annotation { "Feature Type Name" : "Feature", "Feature Type Description" : "" }
export const myFeature = defineFeature(function(context is Context, id is Id, definition is map)
    precondition{}
    {
        {
            var Q0;
            Q0=qCreatedBy(makeId("Top.planeOp"),FACE);
            var sketch = newSketch(context, id + "F0", { "sketchPlane" : qUnion([Q0])});
            skLineSegment(sketch, "E0.bottom", {"start": v(40, -40) * mm, "end": v(-40, -40) * mm, "construction": true});
            skLineSegment(sketch, "E0.top", {"start": v(40, 40) * mm, "end": v(-40, 40) * mm, "construction": true});
            skLineSegment(sketch, "E0.left", {"start": v(40, -40) * mm, "end": v(40, 40) * mm, "construction": true});
            skLineSegment(sketch, "E0.right", {"start": v(-40, -40) * mm, "end": v(-40, 40) * mm, "construction": true});
            skPoint(sketch, "E0.middle", {"position": v(0, 0) * mm});
            skText(sketch, "E1", { "text": "HAPPY", "fontName": "OpenSans-Bold.ttf"});
            skText(sketch, "E2", { "text": "BIRTHDAY", "fontName": "OpenSans-Bold.ttf"});
            skText(sketch, "E3", { "text": "Lily Rose", "fontName": "OpenSans-Bold.ttf"});
            const initialGuessF0  = {"E1": [-0.0375, 0.01154, 1, 0, 0.01588], "E2": [-0.0375, -0.004, 1, 0, 0.01053], "E3": [-0.0375, -0.02129, 1, 0, 0.0123]};
            skSetInitialGuess(sketch, initialGuessF0);
            skSolve(sketch);
        }
        {
            var Q0;
            Q0=makeQuery(id+"F0.imprint","IMPRINT",FACE,{"disambiguationData":[TD([[makeQuery(id+"F0.imprint","IMPRINT",EDGE,{"derivedFrom":sQuery(id+"F0.wireOp",EDGE,"E1.sketch_text.stroke-40")}),-1.0]])]});
            var Q1;
            Q1=makeQuery(id+"F0.imprint","IMPRINT",FACE,{"disambiguationData":[TD([[makeQuery(id+"F0.imprint","IMPRINT",EDGE,{"derivedFrom":sQuery(id+"F0.wireOp",EDGE,"E1.sketch_text.stroke-56")}),-1.0]])]});
            var Q2;
            Q2=makeQuery(id+"F0.imprint","IMPRINT",FACE,{"disambiguationData":[TD([[makeQuery(id+"F0.imprint","IMPRINT",EDGE,{"derivedFrom":sQuery(id+"F0.wireOp",EDGE,"E2.sketch_text.stroke-0")}),-1.0]])]});
            var Q3;
            Q3=makeQuery(id+"F0.imprint","IMPRINT",FACE,{"disambiguationData":[TD([[makeQuery(id+"F0.imprint","IMPRINT",EDGE,{"derivedFrom":sQuery(id+"F0.wireOp",EDGE,"E1.sketch_text.stroke-0")}),-1.0]])]});
            var Q4;
            Q4=makeQuery(id+"F0.imprint","IMPRINT",FACE,{"disambiguationData":[TD([[makeQuery(id+"F0.imprint","IMPRINT",EDGE,{"derivedFrom":sQuery(id+"F0.wireOp",EDGE,"E1.sketch_text.stroke-12")}),-1.0]])]});
            var Q5;
            Q5=makeQuery(id+"F0.imprint","IMPRINT",FACE,{"disambiguationData":[TD([[makeQuery(id+"F0.imprint","IMPRINT",EDGE,{"derivedFrom":sQuery(id+"F0.wireOp",EDGE,"E1.sketch_text.stroke-24")}),-1.0]])]});
            var Q6;
            Q6=makeQuery(id+"F0.imprint","IMPRINT",FACE,{"disambiguationData":[TD([[makeQuery(id+"F0.imprint","IMPRINT",EDGE,{"derivedFrom":sQuery(id+"F0.wireOp",EDGE,"E2.sketch_text.stroke-25")}),-1.0]])]});
            var Q7;
            Q7=makeQuery(id+"F0.imprint","IMPRINT",FACE,{"disambiguationData":[TD([[makeQuery(id+"F0.imprint","IMPRINT",EDGE,{"derivedFrom":sQuery(id+"F0.wireOp",EDGE,"E2.sketch_text.stroke-29")}),-1.0]])]});
            var Q8;
            Q8=makeQuery(id+"F0.imprint","IMPRINT",FACE,{"disambiguationData":[TD([[makeQuery(id+"F0.imprint","IMPRINT",EDGE,{"derivedFrom":sQuery(id+"F0.wireOp",EDGE,"E2.sketch_text.stroke-48")}),-1.0]])]});
            var Q9;
            Q9=makeQuery(id+"F0.imprint","IMPRINT",FACE,{"disambiguationData":[TD([[makeQuery(id+"F0.imprint","IMPRINT",EDGE,{"derivedFrom":sQuery(id+"F0.wireOp",EDGE,"E2.sketch_text.stroke-56")}),-1.0]])]});
            var Q10;
            Q10=makeQuery(id+"F0.imprint","IMPRINT",FACE,{"disambiguationData":[TD([[makeQuery(id+"F0.imprint","IMPRINT",EDGE,{"derivedFrom":sQuery(id+"F0.wireOp",EDGE,"E2.sketch_text.stroke-68")}),-1.0]])]});
            var Q11;
            Q11=makeQuery(id+"F0.imprint","IMPRINT",FACE,{"disambiguationData":[TD([[makeQuery(id+"F0.imprint","IMPRINT",EDGE,{"derivedFrom":sQuery(id+"F0.wireOp",EDGE,"E2.sketch_text.stroke-80")}),-1.0]])]});
            var Q12;
            Q12=makeQuery(id+"F0.imprint","IMPRINT",FACE,{"disambiguationData":[TD([[makeQuery(id+"F0.imprint","IMPRINT",EDGE,{"derivedFrom":sQuery(id+"F0.wireOp",EDGE,"E2.sketch_text.stroke-92")}),-1.0]])]});
            var Q13;
            Q13=makeQuery(id+"F0.imprint","IMPRINT",FACE,{"disambiguationData":[TD([[makeQuery(id+"F0.imprint","IMPRINT",EDGE,{"derivedFrom":sQuery(id+"F0.wireOp",EDGE,"E3.sketch_text.stroke-0")}),-1.0]])]});
            var Q14;
            Q14=makeQuery(id+"F0.imprint","IMPRINT",FACE,{"disambiguationData":[TD([[makeQuery(id+"F0.imprint","IMPRINT",EDGE,{"derivedFrom":sQuery(id+"F0.wireOp",EDGE,"E3.sketch_text.stroke-11")}),-1.0]])]});
            var Q15;
            Q15=makeQuery(id+"F0.imprint","IMPRINT",FACE,{"disambiguationData":[TD([[makeQuery(id+"F0.imprint","IMPRINT",EDGE,{"derivedFrom":sQuery(id+"F0.wireOp",EDGE,"E3.sketch_text.stroke-15")}),-1.0]])]});
            var Q16;
            Q16=makeQuery(id+"F0.imprint","IMPRINT",FACE,{"disambiguationData":[TD([[makeQuery(id+"F0.imprint","IMPRINT",EDGE,{"derivedFrom":sQuery(id+"F0.wireOp",EDGE,"E3.sketch_text.stroke-19")}),-1.0]])]});
            var Q17;
            Q17=makeQuery(id+"F0.imprint","IMPRINT",FACE,{"disambiguationData":[TD([[makeQuery(id+"F0.imprint","IMPRINT",EDGE,{"derivedFrom":sQuery(id+"F0.wireOp",EDGE,"E3.sketch_text.stroke-36")}),-1.0]])]});
            var Q18;
            Q18=makeQuery(id+"F0.imprint","IMPRINT",FACE,{"disambiguationData":[TD([[makeQuery(id+"F0.imprint","IMPRINT",EDGE,{"derivedFrom":sQuery(id+"F0.wireOp",EDGE,"E3.sketch_text.stroke-73")}),-1.0]])]});
            var Q19;
            Q19=makeQuery(id+"F0.imprint","IMPRINT",FACE,{"disambiguationData":[TD([[makeQuery(id+"F0.imprint","IMPRINT",EDGE,{"derivedFrom":sQuery(id+"F0.wireOp",EDGE,"E3.sketch_text.stroke-99")}),-1.0]])]});
            extrude(context, id + "F1", {"entities" : qUnion([Q0, Q1, Q2, Q3, Q4, Q5, Q6, Q7, Q8, Q9, Q10, Q11, Q12, Q13, Q14, Q15, Q16, Q17, Q18, Q19]), "depth" : 4 * mm});
        }
        {
            var Q0;
            Q0=qCreatedBy(makeId("Top.planeOp"),FACE);
            var sketch = newSketch(context, id + "F2", { "sketchPlane" : qUnion([Q0])});
            skLineSegment(sketch, "E4.bottom", {"start": v(-36.19, -3) * mm, "end": v(33.09, -3) * mm});
            skLineSegment(sketch, "E4.top", {"start": v(-36.19, -6) * mm, "end": v(33.09, -6) * mm});
            skLineSegment(sketch, "E4.left", {"start": v(-36.19, -3) * mm, "end": v(-36.19, -6) * mm});
            skLineSegment(sketch, "E4.right", {"start": v(33.09, -3) * mm, "end": v(33.09, -6) * mm});
            skLineSegment(sketch, "E5.bottom", {"start": v(-35.97, -20.15) * mm, "end": v(35.87, -20.15) * mm});
            skLineSegment(sketch, "E5.top", {"start": v(-35.97, -23.15) * mm, "end": v(35.87, -23.15) * mm});
            skLineSegment(sketch, "E5.left", {"start": v(-35.97, -20.15) * mm, "end": v(-35.97, -23.15) * mm});
            skLineSegment(sketch, "E5.right", {"start": v(35.87, -20.15) * mm, "end": v(35.87, -23.15) * mm});
            skLineSegment(sketch, "E6.bottom", {"start": v(-35.52, 12.54) * mm, "end": v(30.84, 12.54) * mm});
            skLineSegment(sketch, "E6.top", {"start": v(-35.52, 9.54) * mm, "end": v(30.84, 9.54) * mm});
            skLineSegment(sketch, "E6.left", {"start": v(-35.52, 12.54) * mm, "end": v(-35.52, 9.54) * mm});
            skLineSegment(sketch, "E6.right", {"start": v(30.84, 12.54) * mm, "end": v(30.84, 9.54) * mm});
            skSolve(sketch);
        }
        {
            var Q0;
            Q0 = qSketchRegion(id + "F2", true);
            extrude(context, id + "F3", {"entities" : qUnion([Q0]), "operationType" : NewBodyOperationType.ADD, "depth" : 2 * mm});
        }
        {
            var Q0;
            Q0=qCreatedBy(makeId("Top.planeOp"),FACE);
            var sketch = newSketch(context, id + "F4", { "sketchPlane" : qUnion([Q0])});
            skArc(sketch, "E7", {"start": v(10.9, 43.1) * mm, "mid": v(5.85, 42.23) * mm, "end": v(5.8, 37.1) * mm});
            skArc(sketch, "E8", {"start": v(15.99, 37.1) * mm, "mid": v(15.95, 42.23) * mm, "end": v(10.9, 43.1) * mm});
            skLineSegment(sketch, "E9", {"start": v(10.73, 31.11) * mm, "end": v(5.8, 37.1) * mm});
            skLineSegment(sketch, "E10", {"start": v(10.73, 31.11) * mm, "end": v(15.99, 37.1) * mm});
            skPoint(sketch, "E11.orphan", {"position": v(10.9, 39.64) * mm});
            skArc(sketch, "E12", {"start": v(20.67, 36.61) * mm, "mid": v(15.62, 35.73) * mm, "end": v(15.58, 30.6) * mm});
            skArc(sketch, "E13", {"start": v(25.76, 30.6) * mm, "mid": v(25.72, 35.73) * mm, "end": v(20.67, 36.61) * mm});
            skLineSegment(sketch, "E14", {"start": v(20.5, 24.62) * mm, "end": v(15.58, 30.6) * mm});
            skLineSegment(sketch, "E15", {"start": v(20.5, 24.62) * mm, "end": v(25.76, 30.6) * mm});
            skPoint(sketch, "E16.orphan", {"position": v(20.67, 33.15) * mm});
            skArc(sketch, "E17", {"start": v(30.02, 33.58) * mm, "mid": v(24.97, 32.7) * mm, "end": v(24.93, 27.58) * mm});
            skArc(sketch, "E18", {"start": v(34.94, 27.38) * mm, "mid": v(35.16, 32.6) * mm, "end": v(30.02, 33.58) * mm});
            skLineSegment(sketch, "E19", {"start": v(29.85, 21.59) * mm, "end": v(24.93, 27.58) * mm});
            skLineSegment(sketch, "E20", {"start": v(29.85, 21.59) * mm, "end": v(34.94, 27.38) * mm});
            skPoint(sketch, "E21.orphan", {"position": v(30.02, 30.12) * mm});
            skArc(sketch, "E22", {"start": v(32.68, 43.38) * mm, "mid": v(27.63, 42.5) * mm, "end": v(27.59, 37.38) * mm});
            skArc(sketch, "E23", {"start": v(37.77, 37.38) * mm, "mid": v(37.73, 42.5) * mm, "end": v(32.68, 43.38) * mm});
            skLineSegment(sketch, "E24", {"start": v(32.5, 31.4) * mm, "end": v(27.59, 37.38) * mm});
            skLineSegment(sketch, "E25", {"start": v(32.5, 31.4) * mm, "end": v(37.77, 37.38) * mm});
            skPoint(sketch, "E26.orphan", {"position": v(32.68, 39.92) * mm});
            skArc(sketch, "E27", {"start": v(23.28, 47.6) * mm, "mid": v(18.23, 46.73) * mm, "end": v(18.2, 41.6) * mm});
            skArc(sketch, "E28", {"start": v(28.37, 41.6) * mm, "mid": v(28.33, 46.73) * mm, "end": v(23.28, 47.6) * mm});
            skLineSegment(sketch, "E29", {"start": v(23.11, 35.61) * mm, "end": v(18.2, 41.6) * mm});
            skLineSegment(sketch, "E30", {"start": v(23.11, 35.61) * mm, "end": v(28.37, 41.6) * mm});
            skPoint(sketch, "E31.orphan", {"position": v(23.28, 44.14) * mm});
            skArc(sketch, "E32", {"start": v(13.68, 51.62) * mm, "mid": v(8.63, 50.75) * mm, "end": v(8.6, 45.62) * mm});
            skArc(sketch, "E33", {"start": v(18.77, 45.62) * mm, "mid": v(18.73, 50.75) * mm, "end": v(13.68, 51.62) * mm});
            skLineSegment(sketch, "E34", {"start": v(13.51, 39.63) * mm, "end": v(8.6, 45.62) * mm});
            skLineSegment(sketch, "E35", {"start": v(13.51, 39.63) * mm, "end": v(18.77, 45.62) * mm});
            skPoint(sketch, "E36.orphan", {"position": v(13.68, 48.16) * mm});
            skArc(sketch, "E37", {"start": v(-25.3, -8.27) * mm, "mid": v(-27.2, -8.6) * mm, "end": v(-27.21, -10.52) * mm});
            skArc(sketch, "E38", {"start": v(-23.46, -10.6) * mm, "mid": v(-23.38, -8.64) * mm, "end": v(-25.3, -8.27) * mm});
            skLineSegment(sketch, "E39", {"start": v(-25.37, -12.77) * mm, "end": v(-27.21, -10.52) * mm});
            skLineSegment(sketch, "E40", {"start": v(-25.37, -12.77) * mm, "end": v(-23.46, -10.6) * mm});
            skPoint(sketch, "E41.orphan", {"position": v(-25.3, -9.57) * mm});
            skArc(sketch, "E42", {"start": v(13.3, -11.78) * mm, "mid": v(8.88, -12.55) * mm, "end": v(8.84, -17.04) * mm});
            skArc(sketch, "E43", {"start": v(17.75, -17.04) * mm, "mid": v(17.72, -12.55) * mm, "end": v(13.3, -11.78) * mm});
            skLineSegment(sketch, "E44", {"start": v(13.15, -22.28) * mm, "end": v(8.84, -17.04) * mm});
            skLineSegment(sketch, "E45", {"start": v(13.15, -22.28) * mm, "end": v(17.75, -17.04) * mm});
            skPoint(sketch, "E46.orphan", {"position": v(13.3, -14.81) * mm});
            skArc(sketch, "E47", {"start": v(32.19, 11.18) * mm, "mid": v(27.14, 10.3) * mm, "end": v(27.1, 5.18) * mm});
            skArc(sketch, "E48", {"start": v(37.28, 5.18) * mm, "mid": v(37.24, 10.3) * mm, "end": v(32.19, 11.18) * mm});
            skLineSegment(sketch, "E49", {"start": v(32.02, -0.8) * mm, "end": v(27.1, 5.18) * mm});
            skLineSegment(sketch, "E50", {"start": v(32.02, -0.8) * mm, "end": v(37.28, 5.18) * mm});
            skPoint(sketch, "E51.orphan", {"position": v(32.19, 7.72) * mm});
            skArc(sketch, "E52", {"start": v(-28.3, 13.84) * mm, "mid": v(-33.35, 12.96) * mm, "end": v(-33.39, 7.84) * mm});
            skArc(sketch, "E53", {"start": v(-23.38, 7.64) * mm, "mid": v(-23.16, 12.86) * mm, "end": v(-28.3, 13.84) * mm});
            skLineSegment(sketch, "E54", {"start": v(-28.47, 1.85) * mm, "end": v(-33.39, 7.84) * mm});
            skLineSegment(sketch, "E55", {"start": v(-28.47, 1.85) * mm, "end": v(-23.38, 7.64) * mm});
            skPoint(sketch, "E56.orphan", {"position": v(-28.3, 10.38) * mm});
            skArc(sketch, "E57", {"start": v(31.8, -3.33) * mm, "mid": v(26.76, -4.2) * mm, "end": v(26.72, -9.33) * mm});
            skArc(sketch, "E58", {"start": v(36.9, -9.33) * mm, "mid": v(36.86, -4.2) * mm, "end": v(31.8, -3.33) * mm});
            skLineSegment(sketch, "E59", {"start": v(31.64, -15.32) * mm, "end": v(26.72, -9.33) * mm});
            skLineSegment(sketch, "E60", {"start": v(31.64, -15.32) * mm, "end": v(36.9, -9.33) * mm});
            skPoint(sketch, "E61.orphan", {"position": v(31.8, -6.8) * mm});
            skArc(sketch, "E62", {"start": v(-32.87, -5.45) * mm, "mid": v(-36.06, -6.05) * mm, "end": v(-35.97, -9.3) * mm});
            skArc(sketch, "E63", {"start": v(-29.8, -9.33) * mm, "mid": v(-29.66, -6.07) * mm, "end": v(-32.87, -5.45) * mm});
            skLineSegment(sketch, "E64", {"start": v(-32.87, -12.73) * mm, "end": v(-35.97, -9.3) * mm});
            skLineSegment(sketch, "E65", {"start": v(-32.87, -12.73) * mm, "end": v(-29.8, -9.33) * mm});
            skPoint(sketch, "E66.orphan", {"position": v(-32.87, -7.62) * mm});
            skArc(sketch, "E67", {"start": v(13.84, 32.95) * mm, "mid": v(8.78, 32.07) * mm, "end": v(8.74, 26.95) * mm});
            skArc(sketch, "E68", {"start": v(18.93, 26.95) * mm, "mid": v(18.89, 32.07) * mm, "end": v(13.84, 32.95) * mm});
            skLineSegment(sketch, "E69", {"start": v(13.66, 20.96) * mm, "end": v(8.74, 26.95) * mm});
            skLineSegment(sketch, "E70", {"start": v(13.66, 20.96) * mm, "end": v(18.93, 26.95) * mm});
            skPoint(sketch, "E71.orphan", {"position": v(13.84, 29.48) * mm});
            skArc(sketch, "E72", {"start": v(-4.5, 10.34) * mm, "mid": v(-7.65, 9.79) * mm, "end": v(-7.67, 6.59) * mm});
            skArc(sketch, "E73", {"start": v(-1.42, 6.46) * mm, "mid": v(-1.28, 9.73) * mm, "end": v(-4.5, 10.34) * mm});
            skLineSegment(sketch, "E74", {"start": v(-4.6, 2.84) * mm, "end": v(-7.67, 6.59) * mm});
            skLineSegment(sketch, "E75", {"start": v(-4.6, 2.84) * mm, "end": v(-1.42, 6.46) * mm});
            skPoint(sketch, "E76.orphan", {"position": v(-4.5, 8.17) * mm});
            skArc(sketch, "E77", {"start": v(6.83, -5.27) * mm, "mid": v(3.68, -5.82) * mm, "end": v(3.65, -9.02) * mm});
            skArc(sketch, "E78", {"start": v(10.01, -9.02) * mm, "mid": v(9.99, -5.82) * mm, "end": v(6.83, -5.27) * mm});
            skLineSegment(sketch, "E79", {"start": v(6.73, -12.77) * mm, "end": v(3.65, -9.02) * mm});
            skLineSegment(sketch, "E80", {"start": v(6.73, -12.77) * mm, "end": v(10.01, -9.02) * mm});
            skPoint(sketch, "E81.orphan", {"position": v(6.83, -7.44) * mm});
            skLineSegment(sketch, "E82", {"start": v(-32.87, -7.62) * mm, "end": v(-32.87, -12.73) * mm});
            skSolve(sketch);
        }
        {
            var Q0;
            Q0 = qSketchRegion(id + "F4", true);
            var Q1;
            {var subQ0=sQuery(id+"F4.wireOp",EDGE,"E30");var subQ1=sQuery(id+"F4.wireOp",EDGE,"E13");var subQ2=makeQuery(id+"F4.imprint","INTERSECT",VERTEX,{"derivedFrom":[subQ1,subQ0]});Q1=makeQuery(id+"F4.imprint","IMPRINT",FACE,{"disambiguationData":[TD([[makeQuery(id+"F4.imprint","IMPRINT",EDGE,{"disambiguationData":[TD([[subQ2,-1.0]])],"derivedFrom":subQ1}),1.0]])]});}
            extrude(context, id + "F5", {"entities" : qUnion([Q0, Q1]), "operationType" : NewBodyOperationType.ADD, "depth" : 3 * mm});
        }
    });